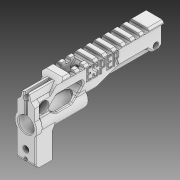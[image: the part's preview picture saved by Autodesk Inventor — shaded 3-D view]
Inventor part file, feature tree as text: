
AUTODESK INVENTOR PART (.ipt)
format: ipt  version: 2020 (Build 240168000, 168)  size: 902,656 bytes
history: native  units: in
note: dims shown in document units (in); Inventor stores cm internally (conversion verified against a paired STEP export)
features: extrude x5, sketch x5, chamfer x2, projected_geometry x1, imported_body x1
ambient origin geometry x8: Origin, YZ Plane, XZ Plane, XY Plane, X Axis, Y Axis, Z Axis, Center Point
bodies: Solid1 (feature_tree)
feature tree (14):
  extrude  "Extrusion1"  Depth=0.0394in TaperAngle=45.0deg
  chamfer  "Chamfer1"  [1 undecoded]
  extrude  "Extrusion2"  Depth=0.3937in TaperAngle=0.0deg
  chamfer  "Chamfer2"  [1 undecoded]
  extrude  "Extrusion3"  Depth=0.1887in TaperAngle=0.0deg
  extrude  "Extrusion4"  [1 undecoded]
  extrude  "Extrusion5"  [1 undecoded]
  sketch  "Sketch1"  dims[d0=0.0in d1=0.0in d2=0.0394in d3=0.0787in d4=45.0deg]
  sketch  "Sketch2"  dims[d6=0.1425in d7=0.0in d8=0.0in]
  sketch  "Sketch3"  dims[d9=0.0394in d10=0.0787in d11=45.0deg d12=0.3937in d13=0.0in]
  sketch  "Sketch4"  dims[d14=0.1378in]
  sketch  "Sketch5"  dims[d15=1.2598in d16=0.0in d17=0.0in d18=0.1887in d19=0.0in]
  projected_geometry  "Projected Loop1"
  imported_body  "Base1"
note: 4 required parameter values undecoded (feature->parameter linkage not recoverable at this tier; creation-order binding heuristic only, values carry confidence <= 0.55)
